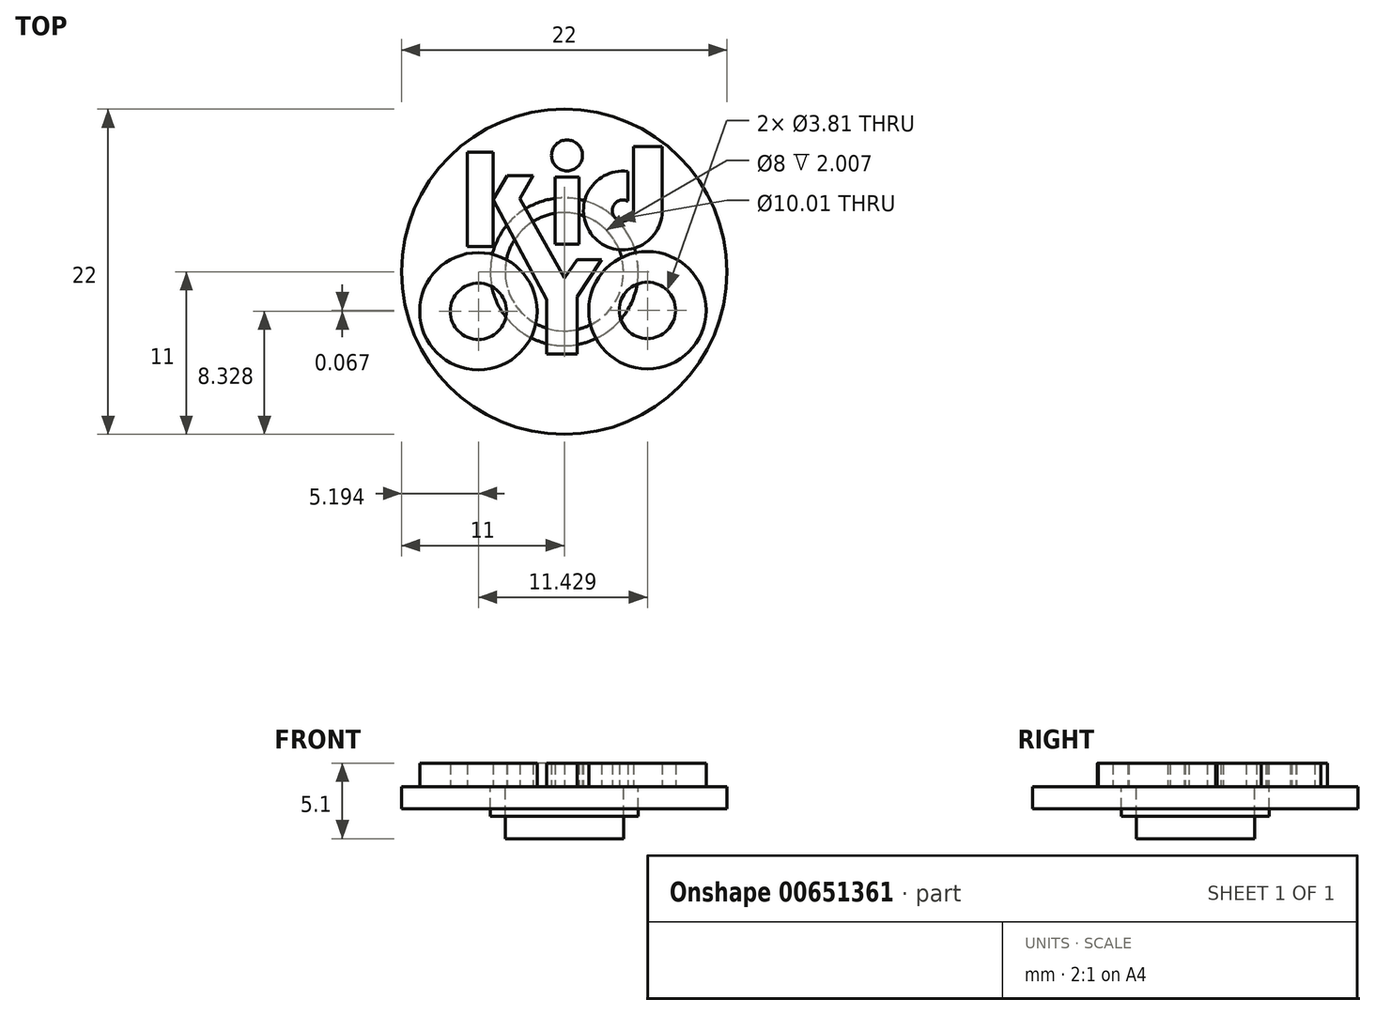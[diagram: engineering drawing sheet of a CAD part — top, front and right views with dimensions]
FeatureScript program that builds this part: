
annotation { "Feature Type Name" : "Feature", "Feature Type Description" : "" }
export const myFeature = defineFeature(function(context is Context, id is Id, definition is map)
    precondition{}
    {
        {
            var Q0;
            Q0=qCreatedBy(makeId("Top.planeOp"),FACE);
            var sketch = newSketch(context, id + "F0", { "sketchPlane" : qUnion([Q0])});
            skCircle(sketch, "E0", {"center": v(0, 0) * mm, "radius": 11 * mm});
            skCircle(sketch, "E1", {"center": v(0, 0) * mm, "radius": 5 * mm});
            skCircle(sketch, "E2", {"center": v(0, 0) * mm, "radius": 4 * mm});
            skSolve(sketch);
        }
        {
            var Q0;
            Q0=makeQuery(id+"F0.imprint","IMPRINT",FACE,{"disambiguationData":[TD([[makeQuery(id+"F0.imprint","IMPRINT",EDGE,{"derivedFrom":sQuery(id+"F0.wireOp",EDGE,"E0")}),1.0]])]});
            extrude(context, id + "F1", {"entities" : qUnion([Q0]), "oppositeDirection" : true, "depth" : 1.5 * mm, "offsetDistance" : 25.4 * mm});
        }
        {
            var Q0;
            Q0=makeQuery(id+"F0.imprint","IMPRINT",FACE,{"disambiguationData":[TD([[makeQuery(id+"F0.imprint","IMPRINT",EDGE,{"derivedFrom":sQuery(id+"F0.wireOp",EDGE,"E1")}),1.0]])]});
            var Q1;
            Q1=sQuery(id+"F0.wireOp",EDGE,"E1");
            extrude(context, id + "F2", {"entities" : qUnion([Q0]), "surfaceEntities" : qUnion([Q1]), "oppositeDirection" : true, "depth" : 2 * mm, "offsetDistance" : 25.4 * mm});
        }
        {
            var Q0;
            Q0=makeQuery(id+"F0.imprint","IMPRINT",FACE,{"disambiguationData":[TD([[makeQuery(id+"F0.imprint","IMPRINT",EDGE,{"derivedFrom":sQuery(id+"F0.wireOp",EDGE,"E2")}),1.0]])]});
            extrude(context, id + "F3", {"entities" : qUnion([Q0]), "oppositeDirection" : true, "depth" : 3.5 * mm, "offsetDistance" : 25.4 * mm});
        }
        {
            var Q0;
            Q0=qCreatedBy(makeId("Top.planeOp"),FACE);
            var sketch = newSketch(context, id + "F4", { "sketchPlane" : qUnion([Q0])});
            skLineSegment(sketch, "E3.bottom", {"start": v(-0.96, -4.46) * mm, "end": v(0.7, -4.46) * mm});
            skLineSegment(sketch, "E3.left", {"start": v(-0.96, -4.46) * mm, "end": v(-0.96, -1.5) * mm});
            skLineSegment(sketch, "E3.right", {"start": v(0.7, -4.46) * mm, "end": v(0.7, -1.35) * mm});
            skLineSegment(sketch, "E4", {"start": v(0.7, -1.35) * mm, "end": v(2.03, 0.65) * mm});
            skLineSegment(sketch, "E5", {"start": v(2.03, 0.65) * mm, "end": v(0.7, 0.65) * mm});
            skLineSegment(sketch, "E6", {"start": v(0.7, 0.65) * mm, "end": v(0, -0.34) * mm});
            skLineSegment(sketch, "E7", {"start": v(0, -0.34) * mm, "end": v(-2.4, 3.96) * mm});
            skLineSegment(sketch, "E8", {"start": v(-2.4, 3.96) * mm, "end": v(-1.7, 5.2) * mm});
            skLineSegment(sketch, "E9", {"start": v(-1.7, 5.2) * mm, "end": v(-3.1, 5.2) * mm});
            skLineSegment(sketch, "E10.bottom", {"start": v(-5.25, 1.37) * mm, "end": v(-3.85, 1.37) * mm});
            skLineSegment(sketch, "E10.top", {"start": v(-5.25, 6.47) * mm, "end": v(-3.85, 6.47) * mm});
            skLineSegment(sketch, "E10.left", {"start": v(-5.25, 1.37) * mm, "end": v(-5.25, 6.47) * mm});
            skLineSegment(sketch, "E11.bottom", {"start": v(-0.5, 1.5) * mm, "end": v(0.8, 1.5) * mm});
            skLineSegment(sketch, "E11.top", {"start": v(-0.5, 5.13) * mm, "end": v(0.8, 5.13) * mm});
            skLineSegment(sketch, "E11.left", {"start": v(-0.5, 1.5) * mm, "end": v(-0.5, 5.13) * mm});
            skLineSegment(sketch, "E11.right", {"start": v(0.8, 1.5) * mm, "end": v(0.8, 5.13) * mm});
            skCircle(sketch, "E12", {"center": v(0.15, 6.3) * mm, "radius": 0.84 * mm});
            skCircle(sketch, "E13", {"center": v(-4.64, -2.14) * mm, "radius": 3.18 * mm});
            skCircle(sketch, "E14", {"center": v(4.5, -2.08) * mm, "radius": 3.18 * mm});
            skCircle(sketch, "E15", {"center": v(4.5, -2.08) * mm, "radius": 1.52 * mm});
            skCircle(sketch, "E16", {"center": v(-4.64, -2.14) * mm, "radius": 1.52 * mm});
            skArc(sketch, "E17", {"start": v(3.43, 5.43) * mm, "mid": v(1.66, 1.81) * mm, "end": v(5.28, 3.57) * mm});
            skArc(sketch, "E18", {"start": v(3.43, 3.82) * mm, "mid": v(2.68, 3.02) * mm, "end": v(3.74, 3.33) * mm});
            skLineSegment(sketch, "E19.top", {"start": v(3.74, 6.78) * mm, "end": v(5.28, 6.78) * mm});
            skLineSegment(sketch, "E19.left", {"start": v(3.74, 5.37) * mm, "end": v(3.74, 6.78) * mm});
            skLineSegment(sketch, "E19.right", {"start": v(5.28, 3.57) * mm, "end": v(5.28, 6.78) * mm});
            skLineSegment(sketch, "E20", {"start": v(3.43, 3.82) * mm, "end": v(3.43, 5.43) * mm});
            skLineSegment(sketch, "E21", {"start": v(3.74, 5.37) * mm, "end": v(3.74, 3.3) * mm});
            skLineSegment(sketch, "E22", {"start": v(-3.85, 6.47) * mm, "end": v(-3.85, 1.37) * mm});
            skLineSegment(sketch, "E23", {"start": v(-3.85, 3.92) * mm, "end": v(-3.1, 5.2) * mm});
            skLineSegment(sketch, "E24", {"start": v(-3.85, 3.92) * mm, "end": v(-0.96, -1.5) * mm});
            skSolve(sketch);
        }
        {
            var Q0;
            Q0 = qSketchRegion(id + "F4", true);
            extrude(context, id + "F5", {"entities" : qUnion([Q0]), "depth" : 1.27 * mm, "offsetDistance" : 25.4 * mm});
        }
        {
            var Q0;
            Q0=makeQuery(id+"F5.opExtrude","SWEPT_BODY",BODY,{"disambiguationData":[OSD([sQuery(id+"F4.wireOp",EDGE,"E10.bottom"),sQuery(id+"F4.wireOp",EDGE,"E10.top"),sQuery(id+"F4.wireOp",EDGE,"E10.left"),sQuery(id+"F4.wireOp",EDGE,"E22")])]});
            var Q1;
            Q1=makeQuery(id+"F5.opExtrude","SWEPT_BODY",BODY,{"disambiguationData":[OSD([sQuery(id+"F4.wireOp",EDGE,"E3.bottom"),sQuery(id+"F4.wireOp",EDGE,"E3.left"),sQuery(id+"F4.wireOp",EDGE,"E3.right"),sQuery(id+"F4.wireOp",EDGE,"E4"),sQuery(id+"F4.wireOp",EDGE,"E5"),sQuery(id+"F4.wireOp",EDGE,"E6"),sQuery(id+"F4.wireOp",EDGE,"E7"),sQuery(id+"F4.wireOp",EDGE,"E8"),sQuery(id+"F4.wireOp",EDGE,"E9"),sQuery(id+"F4.wireOp",EDGE,"E23"),sQuery(id+"F4.wireOp",EDGE,"E24")])]});
            var Q2;
            Q2=makeQuery(id+"F5.opExtrude","SWEPT_BODY",BODY,{"disambiguationData":[OSD([sQuery(id+"F4.wireOp",EDGE,"E11.bottom"),sQuery(id+"F4.wireOp",EDGE,"E11.top"),sQuery(id+"F4.wireOp",EDGE,"E11.left"),sQuery(id+"F4.wireOp",EDGE,"E11.right")])]});
            var Q3;
            Q3=makeQuery(id+"F5.opExtrude","SWEPT_BODY",BODY,{"disambiguationData":[OSD([sQuery(id+"F4.wireOp",EDGE,"E12")])]});
            var Q4;
            Q4=makeQuery(id+"F5.opExtrude","SWEPT_BODY",BODY,{"disambiguationData":[OSD([sQuery(id+"F4.wireOp",EDGE,"E17"),sQuery(id+"F4.wireOp",EDGE,"E18"),sQuery(id+"F4.wireOp",EDGE,"E19.top"),sQuery(id+"F4.wireOp",EDGE,"E19.left"),sQuery(id+"F4.wireOp",EDGE,"E19.right"),sQuery(id+"F4.wireOp",EDGE,"E20"),sQuery(id+"F4.wireOp",EDGE,"E21")])]});
            var Q5;
            Q5=makeQuery(id+"F5.opExtrude","SWEPT_BODY",BODY,{"disambiguationData":[OSD([sQuery(id+"F4.wireOp",EDGE,"E14"),sQuery(id+"F4.wireOp",EDGE,"E15")])]});
            var Q6;
            Q6=makeQuery(id+"F5.opExtrude","SWEPT_BODY",BODY,{"disambiguationData":[OSD([sQuery(id+"F4.wireOp",EDGE,"E13"),sQuery(id+"F4.wireOp",EDGE,"E16")])]});
            var Q7;
            Q7=qCreatedBy(makeId("Origin.pointOp"),VERTEX);
            transform(context, id + "F6", {"entities" : qUnion([Q0, Q1, Q2, Q3, Q4, Q5, Q6]), "transformType" : TransformType.SCALE_UNIFORMLY, "scale" : 1.25, "scalePoint" : qUnion([Q7]), "makeCopy" : false});
        }
    });
